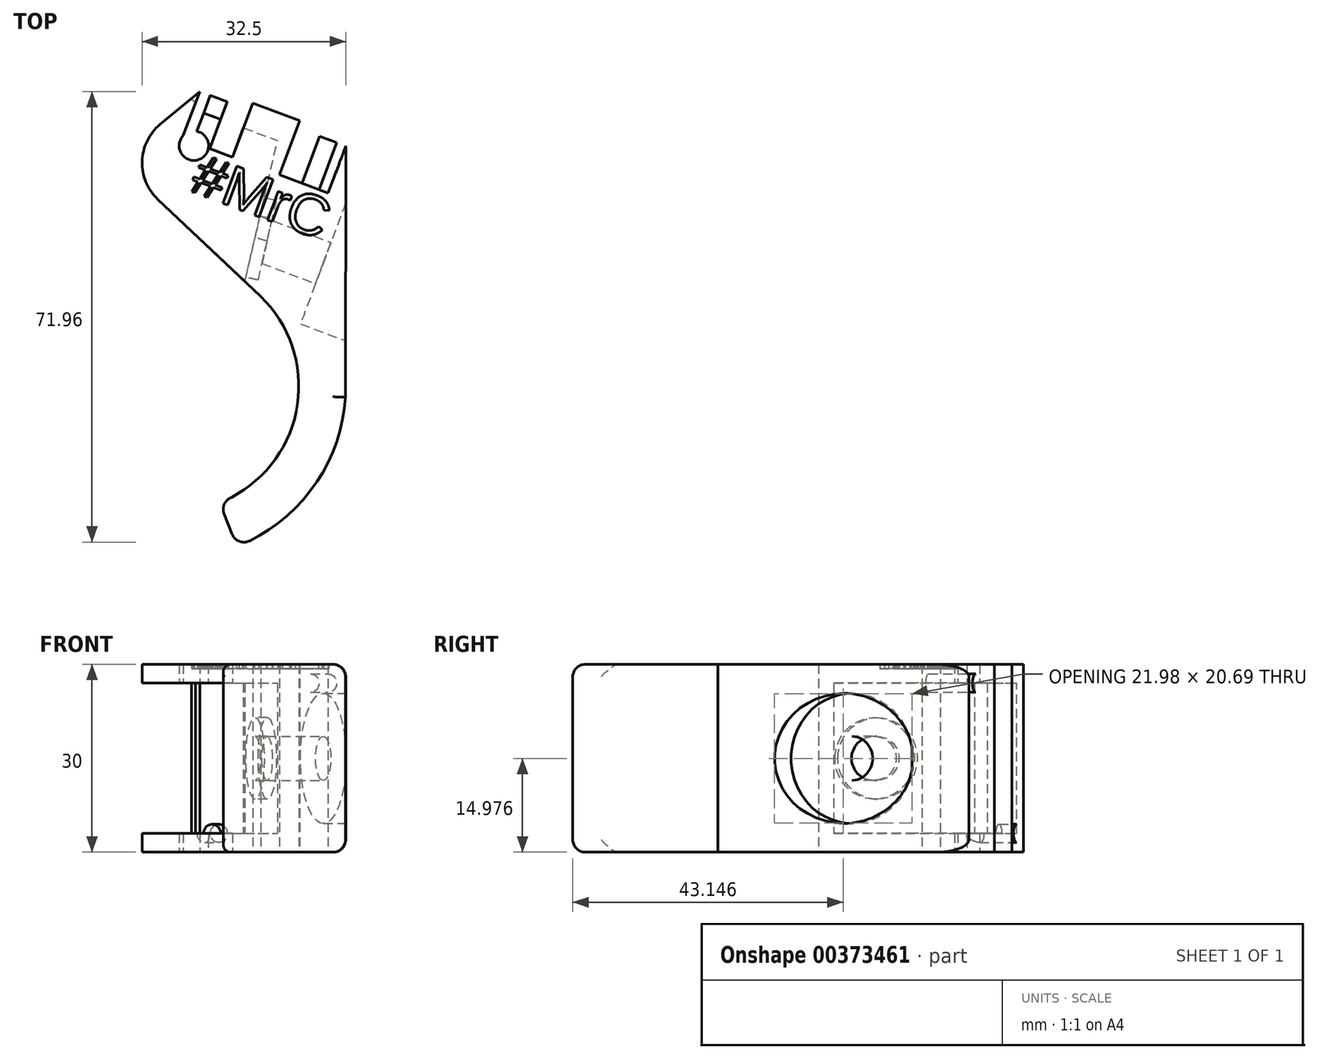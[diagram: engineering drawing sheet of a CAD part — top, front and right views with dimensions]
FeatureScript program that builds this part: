
annotation { "Feature Type Name" : "Feature", "Feature Type Description" : "" }
export const myFeature = defineFeature(function(context is Context, id is Id, definition is map)
    precondition{}
    {
        {
            var Q0;
            Q0=qCreatedBy(makeId("Top.planeOp"),FACE);
            var sketch = newSketch(context, id + "F0", { "sketchPlane" : qUnion([Q0])});
            skCircle(sketch, "E0", {"center": v(0, 0) * mm, "radius": 18 * mm, "construction": true});
            skArc(sketch, "E1", {"start": v(13.42, -14.83) * mm, "mid": v(19.74, 3.2) * mm, "end": v(8.03, 18.32) * mm});
            skArc(sketch, "E2", {"start": v(18.45, -20.39) * mm, "mid": v(26.9, -5.68) * mm, "end": v(25.12, 11.18) * mm});
            skLineSegment(sketch, "E3", {"start": v(26.32, 7.98) * mm, "end": v(12.32, 45.56) * mm});
            skLineSegment(sketch, "E4", {"start": v(-12.55, 45.56) * mm, "end": v(-21.12, 30.6) * mm});
            skLineSegment(sketch, "E5", {"start": v(-21.12, 30.6) * mm, "end": v(8.03, 18.32) * mm});
            skCircle(sketch, "E6", {"center": v(-10.4, 37.12) * mm, "radius": 2.35 * mm});
            skLineSegment(sketch, "E7", {"start": v(-12.55, 45.56) * mm, "end": v(12.32, 45.56) * mm});
            skPoint(sketch, "E8", {"position": v(19.29, 26.85) * mm});
            skLineSegment(sketch, "E9", {"start": v(8.03, 18.32) * mm, "end": v(4.43, 45.56) * mm});
            skLineSegment(sketch, "E10", {"start": v(27.5, 0) * mm, "end": v(27.5, 46.36) * mm});
            skPoint(sketch, "E11", {"position": v(27.5, 26.85) * mm});
            skPoint(sketch, "E12.trimOffspring.end.orphan", {"position": v(12.27, -24.6) * mm});
            skLineSegment(sketch, "E13.trimOffspring", {"start": v(13.42, -14.83) * mm, "end": v(18.45, -20.39) * mm});
            skPoint(sketch, "E14.orphan", {"position": v(22.27, -24.6) * mm});
            skSolve(sketch);
        }
        {
            var Q0;
            {var subQ10=sQuery(id+"F0.wireOp",EDGE,"E4");Q0=makeQuery(id+"F0.imprint","IMPRINT",FACE,{"disambiguationData":[TD([[makeQuery(id+"F0.imprint","IMPRINT",EDGE,{"derivedFrom":subQ10}),1.0]])]});}
            var Q1;
            Q1=makeQuery(id+"F0.imprint","IMPRINT",FACE,{"disambiguationData":[TD([[makeQuery(id+"F0.imprint","IMPRINT",EDGE,{"derivedFrom":sQuery(id+"F0.wireOp",EDGE,"E6")}),1.0]])]});
            extrude(context, id + "F1", {"entities" : qUnion([Q0, Q1]), "depth" : 30 * mm});
        }
        {
            var Q0;
            Q0=makeQuery(id+"F1.opExtrude","SWEPT_FACE",FACE,{"disambiguationData":[OSD([sQuery(id+"F0.wireOp",EDGE,"E5")])]});
            var Q1;
            Q1=makeQuery(id+"F1.opExtrude","SWEPT_FACE",FACE,{"disambiguationData":[OSD([sQuery(id+"F0.wireOp",EDGE,"E1")])]});
            shell(context, id + "F2", {"entities" : qUnion([Q0, Q1]), "thickness" : 3 * mm});
        }
        {
            var Q0;
            Q0=makeQuery(id+"F0.imprint","IMPRINT",FACE,{"disambiguationData":[TD([[makeQuery(id+"F0.imprint","IMPRINT",EDGE,{"derivedFrom":sQuery(id+"F0.wireOp",EDGE,"E1")}),-1.0]])]});
            extrude(context, id + "F3", {"entities" : qUnion([Q0]), "operationType" : NewBodyOperationType.ADD, "depth" : 30 * mm});
        }
        {
            var Q0;
            Q0=makeQuery(id+"F0.imprint","IMPRINT",FACE,{"disambiguationData":[TD([[makeQuery(id+"F0.imprint","IMPRINT",EDGE,{"derivedFrom":sQuery(id+"F0.wireOp",EDGE,"E6")}),1.0]])]});
            extrude(context, id + "F4", {"entities" : qUnion([Q0]), "operationType" : NewBodyOperationType.REMOVE, "depth" : 30 * mm});
        }
        {
            var Q0;
            Q0=qCreatedBy(makeId("Top.planeOp"),FACE);
            var Q1;
            Q1=sQuery(id+"F0.wireOp",EDGE,"E10");
            cPlane(context, id + "F5", {"entities" : qUnion([Q0, Q1]), "cplaneType" : CPlaneType.LINE_ANGLE, "offset" : 25 * mm, "angle" : 90 * degree, "width" : 150 * mm, "height" : 150 * mm});
        }
        {
            var Q0;
            Q0=qCreatedBy(id+"F5.planeOp",FACE);
            var sketch = newSketch(context, id + "F6", { "sketchPlane" : qUnion([Q0])});
            skCircle(sketch, "E15", {"center": v(-26.8, 14.98) * mm, "radius": 3.5 * mm});
            skCircle(sketch, "E16", {"center": v(-26.8, 14.98) * mm, "radius": 10.39 * mm});
            skSolve(sketch);
        }
        {
            var Q0;
            Q0=makeQuery(id+"F6.imprint","IMPRINT",FACE,{"disambiguationData":[TD([[makeQuery(id+"F6.imprint","IMPRINT",EDGE,{"derivedFrom":sQuery(id+"F6.wireOp",EDGE,"E15")}),1.0]])]});
            extrude(context, id + "F7", {"entities" : qUnion([Q0]), "operationType" : NewBodyOperationType.REMOVE, "depth" : 25 * mm});
        }
        {
            var Q0;
            Q0=makeQuery(id+"F6.imprint","IMPRINT",FACE,{"disambiguationData":[TD([[makeQuery(id+"F6.imprint","IMPRINT",EDGE,{"derivedFrom":sQuery(id+"F6.wireOp",EDGE,"E15")}),-1.0]])]});
            extrude(context, id + "F8", {"entities" : qUnion([Q0]), "operationType" : NewBodyOperationType.REMOVE, "depth" : 12 * mm});
        }
        {
            var Q0;
            Q0=makeQuery(id+"F1.opExtrude","SWEPT_FACE",FACE,{"disambiguationData":[OSD([sQuery(id+"F0.wireOp",EDGE,"E4")])]});
            var sketch = newSketch(context, id + "F9", { "sketchPlane" : qUnion([Q0])});
            skLineSegment(sketch, "E17", {"start": v(-16.05, 3) * mm, "end": v(-31.56, 3) * mm});
            skPoint(sketch, "E18.endSnap0", {"position": v(-16.05, 15) * mm});
            skLineSegment(sketch, "E19.MirrorCS", {"start": v(-16.05, 27) * mm, "end": v(-31.56, 27) * mm});
            skLineSegment(sketch, "E20", {"start": v(-31.56, 3) * mm, "end": v(-31.56, 27) * mm});
            skLineSegment(sketch, "E21", {"start": v(-16.05, 3) * mm, "end": v(-16.05, 27) * mm});
            skSolve(sketch);
        }
        {
            var Q0;
            {var subQ2=sQuery(id+"F0.wireOp",EDGE,"E5");var subQ3=sQuery(id+"F0.wireOp",EDGE,"E4");Q0=makeQuery(id+"Fo4RThrDmYk9kfO_1.boolean.opBoolean","SPLIT",EDGE,{"disambiguationData":[TD([makeQuery(id+"Fo4RThrDmYk9kfO_1.opExtrude","SWEPT_FACE",FACE,{"disambiguationData":[OSD([sQuery(id+"F9.wireOp",EDGE,"E19.MirrorCS")])]})])],"derivedFrom":makeQuery(id+"F1.opExtrude","SWEPT_EDGE",EDGE,{"disambiguationData":[OSD([subQ3,subQ2])]})});}
            var Q1;
            {var subQ2=sQuery(id+"F0.wireOp",EDGE,"E5");var subQ3=sQuery(id+"F0.wireOp",EDGE,"E4");Q1=makeQuery(id+"Fo4RThrDmYk9kfO_1.boolean.opBoolean","SPLIT",EDGE,{"disambiguationData":[TD([makeQuery(id+"Fo4RThrDmYk9kfO_1.opExtrude","SWEPT_FACE",FACE,{"disambiguationData":[OSD([sQuery(id+"F9.wireOp",EDGE,"E17")])]})])],"derivedFrom":makeQuery(id+"F1.opExtrude","SWEPT_EDGE",EDGE,{"disambiguationData":[OSD([subQ3,subQ2])]})});}
            fillet(context, id + "F10", {"entities" : qUnion([Q0, Q1]), "radius" : 8 * mm, "tangentPropagation" : true, "allowEdgeOverflow" : false});
        }
        {
            var Q0;
            Q0=makeQuery(id+"F9.imprint","IMPRINT",FACE,{"disambiguationData":[TD([[makeQuery(id+"F9.imprint","IMPRINT",EDGE,{"derivedFrom":sQuery(id+"F9.wireOp",EDGE,"E17")}),-1.0]])]});
            extrude(context, id + "F11", {"entities" : qUnion([Q0]), "operationType" : NewBodyOperationType.REMOVE, "oppositeDirection" : true, "depth" : 3 * mm});
        }
        {
            var Q0;
            {var subQ0=sQuery(id+"F0.wireOp",EDGE,"E7");Q0=makeQuery(id+"F3.boolean.opBoolean","MERGE",FACE,{"derivedFrom":[makeQuery(id+"F1.opExtrude","SWEPT_FACE",FACE,{"disambiguationData":[OSD([subQ0])]}),makeQuery(id+"F3.opExtrude","SWEPT_FACE",FACE,{"disambiguationData":[OSD([subQ0])]})]});}
            var sketch = newSketch(context, id + "F12", { "sketchPlane" : qUnion([Q0])});
            skLineSegment(sketch, "E22", {"start": v(-12.32, 30) * mm, "end": v(12.55, 30) * mm});
            skLineSegment(sketch, "E23", {"start": v(12.55, 30) * mm, "end": v(12.55, 0) * mm});
            skLineSegment(sketch, "E24", {"start": v(12.55, 0) * mm, "end": v(-12.32, 0) * mm});
            skLineSegment(sketch, "E25", {"start": v(-12.32, 0) * mm, "end": v(-12.32, 30) * mm});
            skCircle(sketch, "E26", {"center": v(-9.32, 3) * mm, "radius": 1.45 * mm});
            skCircle(sketch, "E27.MirrorC", {"center": v(9.32, 3) * mm, "radius": 1.45 * mm});
            skCircle(sketch, "E28.MirrorC", {"center": v(-9.32, 27) * mm, "radius": 1.45 * mm});
            skCircle(sketch, "E29.MirrorC", {"center": v(9.32, 27) * mm, "radius": 1.45 * mm});
            skLineSegment(sketch, "E30", {"start": v(-4, 30) * mm, "end": v(-4, 0) * mm});
            skLineSegment(sketch, "E31.MirrorCS", {"start": v(4, 30) * mm, "end": v(4, 0) * mm});
            skSolve(sketch);
        }
        {
            var Q0;
            Q0=makeQuery(id+"F12.imprint","IMPRINT",FACE,{"disambiguationData":[TD([[makeQuery(id+"F12.imprint","IMPRINT",EDGE,{"derivedFrom":sQuery(id+"F12.wireOp",EDGE,"E27.MirrorC")}),-1.0]])]});
            var Q1;
            Q1=makeQuery(id+"F12.imprint","IMPRINT",FACE,{"disambiguationData":[TD([[makeQuery(id+"F12.imprint","IMPRINT",EDGE,{"derivedFrom":sQuery(id+"F12.wireOp",EDGE,"E29.MirrorC")}),1.0]])]});
            var Q2;
            Q2=makeQuery(id+"F12.imprint","IMPRINT",FACE,{"disambiguationData":[TD([[makeQuery(id+"F12.imprint","IMPRINT",EDGE,{"derivedFrom":sQuery(id+"F12.wireOp",EDGE,"E28.MirrorC")}),-1.0]])]});
            var Q3;
            Q3=makeQuery(id+"F12.imprint","IMPRINT",FACE,{"disambiguationData":[TD([[makeQuery(id+"F12.imprint","IMPRINT",EDGE,{"derivedFrom":sQuery(id+"F12.wireOp",EDGE,"E26")}),1.0]])]});
            extrude(context, id + "F13", {"entities" : qUnion([Q0, Q1, Q2, Q3]), "operationType" : NewBodyOperationType.REMOVE, "oppositeDirection" : true, "depth" : 8 * mm});
        }
        {
            var Q0;
            {var subQ0=sQuery(id+"F12.wireOp",EDGE,"E30");Q0=makeQuery(id+"F12.imprint","IMPRINT",FACE,{"disambiguationData":[TD([[makeQuery(id+"F12.imprint","IMPRINT",EDGE,{"derivedFrom":subQ0}),1.0]])]});}
            extrude(context, id + "F14", {"entities" : qUnion([Q0]), "operationType" : NewBodyOperationType.ADD, "depth" : 1.2 * mm});
        }
        {
            var Q0;
            {var subQ0=sQuery(id+"F0.wireOp",EDGE,"E9");var subQ1=sQuery(id+"F0.wireOp",EDGE,"E7");Q0=makeQuery(id+"F14.boolean.opBoolean","MERGE",FACE,{"derivedFrom":[makeQuery(id+"F3.boolean.opBoolean","MERGE",FACE,{"derivedFrom":[makeQuery(id+"F1.opExtrude","CAP_FACE",FACE,{"disambiguationData":[OSD([sQuery(id+"F0.wireOp",EDGE,"E4"),sQuery(id+"F0.wireOp",EDGE,"E5"),subQ1,subQ0])],"isStart":false}),makeQuery(id+"F3.opExtrude","CAP_FACE",FACE,{"disambiguationData":[OSD([sQuery(id+"F0.wireOp",EDGE,"E1"),sQuery(id+"F0.wireOp",EDGE,"E2"),sQuery(id+"F0.wireOp",EDGE,"E3"),subQ1,subQ0,sQuery(id+"F0.wireOp",EDGE,"E13.trimOffspring")])],"isStart":false})]}),makeQuery(id+"F14.opExtrude","SWEPT_FACE",FACE,{"disambiguationData":[OSD([sQuery(id+"F12.wireOp",EDGE,"E22")])]})]});}
            var sketch = newSketch(context, id + "F15", { "sketchPlane" : qUnion([Q0])});
            skText(sketch, "E32", { "text": "#MrC", "fontName": "Arimo-Regular.ttf"});
            const initialGuessF15  = {"E32": [-0.00871, 0.03012, 1, 0, 0.00665]};
            skSetInitialGuess(sketch, initialGuessF15);
            skSolve(sketch);
        }
        {
            var Q0;
            Q0=makeQuery(id+"F15.imprint","IMPRINT",FACE,{"disambiguationData":[TD([[makeQuery(id+"F15.imprint","IMPRINT",EDGE,{"derivedFrom":sQuery(id+"F15.wireOp",EDGE,"E32.sketch_text.stroke-69")}),-1.0]])]});
            var Q1;
            Q1=makeQuery(id+"F15.imprint","IMPRINT",FACE,{"disambiguationData":[TD([[makeQuery(id+"F15.imprint","IMPRINT",EDGE,{"derivedFrom":sQuery(id+"F15.wireOp",EDGE,"E32.sketch_text.stroke-55")}),-1.0]])]});
            var Q2;
            Q2=makeQuery(id+"F15.imprint","IMPRINT",FACE,{"disambiguationData":[TD([[makeQuery(id+"F15.imprint","IMPRINT",EDGE,{"derivedFrom":sQuery(id+"F15.wireOp",EDGE,"E32.sketch_text.stroke-32")}),-1.0]])]});
            var Q3;
            Q3=makeQuery(id+"F15.imprint","IMPRINT",FACE,{"disambiguationData":[TD([[makeQuery(id+"F15.imprint","IMPRINT",EDGE,{"derivedFrom":sQuery(id+"F15.wireOp",EDGE,"E32.sketch_text.stroke-0")}),-1.0]])]});
            extrude(context, id + "F16", {"entities" : qUnion([Q0, Q1, Q2, Q3]), "operationType" : NewBodyOperationType.REMOVE, "oppositeDirection" : true, "depth" : 0.7 * mm});
        }
        {
            var Q0;
            Q0=makeQuery(id+"F3.opExtrude","SWEPT_EDGE",EDGE,{"disambiguationData":[OSD([sQuery(id+"F0.wireOp",EDGE,"E1"),sQuery(id+"F0.wireOp",EDGE,"E13.trimOffspring")])]});
            var Q1;
            Q1=makeQuery(id+"F3.opExtrude","SWEPT_EDGE",EDGE,{"disambiguationData":[OSD([sQuery(id+"F0.wireOp",EDGE,"E2"),sQuery(id+"F0.wireOp",EDGE,"E13.trimOffspring")])]});
            var Q2;
            Q2=makeQuery(id+"F3.opExtrude","CAP_EDGE",EDGE,{"disambiguationData":[OSD([sQuery(id+"F0.wireOp",EDGE,"E13.trimOffspring")])],"isStart":true});
            var Q3;
            Q3=makeQuery(id+"F3.opExtrude","CAP_EDGE",EDGE,{"disambiguationData":[OSD([sQuery(id+"F0.wireOp",EDGE,"E13.trimOffspring")])],"isStart":false});
            fillet(context, id + "F17", {"entities" : qUnion([Q0, Q1, Q2, Q3]), "radius" : 2 * mm, "tangentPropagation" : true, "allowEdgeOverflow" : false});
        }
        {
            var Q0;
            Q0=makeQuery(id+"F3.opExtrude","CAP_EDGE",EDGE,{"disambiguationData":[OSD([sQuery(id+"F0.wireOp",EDGE,"E3")])],"isStart":false});
            var Q1;
            Q1=makeQuery(id+"F3.opExtrude","CAP_EDGE",EDGE,{"disambiguationData":[OSD([sQuery(id+"F0.wireOp",EDGE,"E3")])],"isStart":true});
            var Q2;
            Q2=makeQuery(id+"F3.opExtrude","CAP_EDGE",EDGE,{"disambiguationData":[OSD([sQuery(id+"F0.wireOp",EDGE,"E2")])],"isStart":false});
            var Q3;
            Q3=makeQuery(id+"F3.opExtrude","CAP_EDGE",EDGE,{"disambiguationData":[OSD([sQuery(id+"F0.wireOp",EDGE,"E2")])],"isStart":true});
            fillet(context, id + "F18", {"entities" : qUnion([Q0, Q1, Q2, Q3]), "radius" : 2 * mm, "tangentPropagation" : true, "allowEdgeOverflow" : false});
        }
        {
            var Q0;
            Q0=makeQuery(id+"F2.opShell","OFFSET_FACE",FACE,{"disambiguationData":[OSD([sQuery(id+"F0.wireOp",EDGE,"E9")])]});
            var sketch = newSketch(context, id + "F19", { "sketchPlane" : qUnion([Q0])});
            skCircle(sketch, "E33", {"center": v(-26.07, 14.98) * mm, "radius": 6.5 * mm});
            skSolve(sketch);
        }
        {
            var Q0;
            Q0=makeQuery(id+"F19.imprint","IMPRINT",FACE,{"disambiguationData":[TD([[makeQuery(id+"F19.imprint","IMPRINT",EDGE,{"derivedFrom":sQuery(id+"F19.wireOp",EDGE,"E33")}),1.0]])]});
            extrude(context, id + "F20", {"entities" : qUnion([Q0]), "operationType" : NewBodyOperationType.REMOVE, "oppositeDirection" : true, "depth" : 2 * mm});
        }
        {
            var Q0;
            Q0=makeQuery(id+"F1.opExtrude","SWEPT_BODY",BODY,{"disambiguationData":[OSD([sQuery(id+"F0.wireOp",EDGE,"E4"),sQuery(id+"F0.wireOp",EDGE,"E5"),sQuery(id+"F0.wireOp",EDGE,"E7"),sQuery(id+"F0.wireOp",EDGE,"E9")])]});
            var Q1;
            Q1=sQuery(id+"F0.wireOp",EDGE,"E0");
            transform(context, id + "F21", {"entities" : qUnion([Q0]), "transformType" : TransformType.ROTATION, "transformAxis" : qUnion([Q1]), "angle" : 20.5 * degree, "oppositeDirection" : true, "makeCopy" : false});
        }
        {
            var Q0;
            {var subQ0=sQuery(id+"F0.wireOp",EDGE,"E9");var subQ1=sQuery(id+"F0.wireOp",EDGE,"E7");Q0=makeQuery(id+"F14.boolean.opBoolean","MERGE",FACE,{"derivedFrom":[makeQuery(id+"F3.boolean.opBoolean","MERGE",FACE,{"derivedFrom":[makeQuery(id+"F1.opExtrude","CAP_FACE",FACE,{"disambiguationData":[OSD([sQuery(id+"F0.wireOp",EDGE,"E4"),sQuery(id+"F0.wireOp",EDGE,"E5"),subQ1,subQ0])],"isStart":true}),makeQuery(id+"F3.opExtrude","CAP_FACE",FACE,{"disambiguationData":[OSD([sQuery(id+"F0.wireOp",EDGE,"E1"),sQuery(id+"F0.wireOp",EDGE,"E2"),sQuery(id+"F0.wireOp",EDGE,"E3"),subQ1,subQ0,sQuery(id+"F0.wireOp",EDGE,"E13.trimOffspring")])],"isStart":true})]}),makeQuery(id+"F14.opExtrude","SWEPT_FACE",FACE,{"disambiguationData":[OSD([sQuery(id+"F12.wireOp",EDGE,"E24")])]})]});}
            var sketch = newSketch(context, id + "F22", { "sketchPlane" : qUnion([Q0])});
            skLineSegment(sketch, "E34", {"start": v(8.22, -44.03) * mm, "end": v(22.15, -44.03) * mm});
            skLineSegment(sketch, "E35", {"start": v(22.15, -44.03) * mm, "end": v(22.13, -24.27) * mm});
            skLineSegment(sketch, "E36", {"start": v(22.13, -24.27) * mm, "end": v(25.5, -15.7) * mm});
            skLineSegment(sketch, "E37", {"start": v(25.5, -15.7) * mm, "end": v(7.78, -32.42) * mm});
            skArc(sketch, "E38", {"start": v(8.22, -44.03) * mm, "mid": v(10.76, -38.12) * mm, "end": v(7.78, -32.42) * mm});
            skSolve(sketch);
        }
        {
            var Q0;
            Q0=makeQuery(id+"F22.imprint","IMPRINT",FACE,{"disambiguationData":[TD([[makeQuery(id+"F22.imprint","IMPRINT",EDGE,{"derivedFrom":sQuery(id+"F22.wireOp",EDGE,"E34")}),1.0]])]});
            extrude(context, id + "F23", {"entities" : qUnion([Q0]), "operationType" : NewBodyOperationType.REMOVE, "oppositeDirection" : true, "depth" : 0.7 * mm});
        }
        {
            var Q0;
            Q0=makeQuery(id+"F1.opExtrude","SWEPT_BODY",BODY,{"disambiguationData":[OSD([sQuery(id+"F0.wireOp",EDGE,"E4"),sQuery(id+"F0.wireOp",EDGE,"E5"),sQuery(id+"F0.wireOp",EDGE,"E7"),sQuery(id+"F0.wireOp",EDGE,"E9")])]});
            transform(context, id + "F24", {"entities" : qUnion([Q0]), "transformType" : TransformType.TRANSLATION_3D, "dx" : 0 * mm, "dy" : 0 * mm, "dz" : 0 * mm, "makeCopy" : true});
        }
    });
